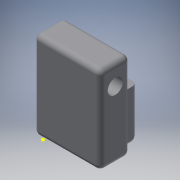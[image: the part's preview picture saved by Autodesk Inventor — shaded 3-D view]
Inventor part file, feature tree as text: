
AUTODESK INVENTOR PART (.ipt)
format: ipt  version: 2018 (Build 220112000, 112)  size: 630,784 bytes
history: native  units: in
note: dims shown in document units (in); Inventor stores cm internally (conversion verified against a paired STEP export)
features: extrude x21, sketch x21, projected_geometry x7, fillet x5, other x4, plane x3, reference x2
ambient origin geometry x8: Origin, YZ Plane, XZ Plane, XY Plane, X Axis, Y Axis, Z Axis, Center Point
bodies: Body1 (feature_tree)
feature tree (63):
  extrude  "Extrusion2"  Depth=0.435in
  sketch  "Sketch3"  dims[d6=0.385in d7=0.0in d9=0.092in]
  extrude  "Extrusion6"  Depth=0.092in
  extrude  "Extrusion7"  Depth=0.1in
  extrude  "Extrusion8"  Depth=0.5814in
  extrude  "Extrusion9"  Depth=7.874in
  extrude  "Extrusion10"  Depth=0.05in
  extrude  "Extrusion11"  Depth=0.15in
  extrude  "Extrusion12"  Depth=0.4in
  extrude  "Extrusion13"  Depth=0.385in TaperAngle=0.0deg
  extrude  "Extrusion14"  Depth=2.5in
  extrude  "Extrusion15"  Depth=0.25in
  extrude  "Extrusion16"  Depth=0.0394in TaperAngle=0.0deg
  extrude  "Extrusion17"  Depth=0.0984in
  extrude  "Extrusion18"  Depth=1.0in TaperAngle=0.0deg
  extrude  "Extrusion19"  Depth=0.0472in TaperAngle=0.0deg
  fillet  "Fillet2"  Radius=0.1177in
  extrude  "Extrusion20"  Depth=0.3937in
  extrude  "Extrusion21"  Depth=0.0787in TaperAngle=0.0deg
  sketch  "Sketch21"  dims[d114=0.3937in d115=0.0787in d116=0.0in]
  plane  "Work Plane1"
  plane  "Work Plane2"
  extrude  "Extrusion23"  Depth=0.0394in
  sketch  "Sketch22"  dims[d117=1.0in d118=0.0in d119=0.0394in]
  sketch  "Sketch23"  dims[d120=1.0in d121=0.5in d122=0.0in d123=0.0in d124=0.2362in d125=0.0in]
  plane  "Work Plane3"
  extrude  "Extrusion24"  Depth=0.2362in TaperAngle=0.0deg
  extrude  "Extrusion25"  Depth=100.0in TaperAngle=0.0deg
  extrude  "Extrusion26"  Depth=0.1575in
  fillet  "Fillet3"  Radius=0.1181in
  fillet  "Fillet4"  Radius=13.0in
  fillet  "Fillet5"  Radius=0.0394in
  fillet  "Fillet6"  Radius=0.0394in
  sketch  "Sketch2"  dims[d4=2.5in d5=0.435in]
  sketch  "Sketch5"  dims[d58=0.1in d59=0.0in d60=0.1in]
  projected_geometry  "Projected Loop1"
  projected_geometry  "Projected Loop2"
  projected_geometry  "Projected Loop3"
  sketch  "Sketch7"  dims[d61=0.385in d62=0.0in d63=0.5814in]
  sketch  "Sketch8"  dims[d64=0.5814in d72=7.874in d74=0.1271in d75=0.3937in d77=1.0in]
  sketch  "Sketch9"  dims[d79=0.25in d80=0.0in d81=0.05in]
  sketch  "Sketch10"  dims[d82=0.385in d83=0.0in d84=0.15in]
  sketch  "Sketch11"  dims[d85=0.05in d86=0.4in]
  projected_geometry  "Projected Loop5"
  sketch  "Sketch12"  dims[d87=0.385in d88=0.0in d89=0.385in d90=0.0in]
  projected_geometry  "Projected Loop6"
  sketch  "Sketch13"  dims[d91=1.0in d92=0.0in d93=2.5in]
  sketch  "Sketch14"  dims[d95=0.1378in d96=0.0in d97=0.25in]
  sketch  "Sketch15"  dims[d98=0.25in d99=0.0394in d100=0.0in]
  sketch  "Sketch16"  dims[d101=0.0984in d102=0.0984in]
  reference  "Reference1"
  sketch  "Sketch17"  dims[d103=0.0394in d104=0.0in d106=1.0in d107=0.0in]
  reference  "Reference2"
  sketch  "Sketch18"  dims[d108=0.0591in d109=0.0472in d110=0.0in d111=0.1177in]
  projected_geometry  "Projected Loop7"
  sketch  "Sketch19"  dims[d112=0.1177in d113=0.3937in]
  sketch  "Sketch24"  dims[d129=100.0in d130=0.0in d131=100.0in d132=0.0in]
  projected_geometry  "Projected Loop8"
  sketch  "Sketch25"  dims[d133=0.2953in d134=0.0in d135=0.1575in d136=0.1181in d137=13.0in d138=0.0in d139=0.0394in d140=0.0394in d141=0.0394in d142=0.0394in]
  other  "<userpath>\OneDrive\Documents\Inventor\TSA\2018\Animatronics\Tortoise\TurtleAssembly2.iam"
  other  "TurtleAssembly2.iam"
  other  "SyringEnd:5"
  other  "SyringEnd:4"
